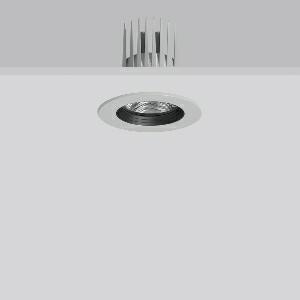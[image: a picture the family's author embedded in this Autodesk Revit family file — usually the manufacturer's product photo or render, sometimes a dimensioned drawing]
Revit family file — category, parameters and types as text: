
# Revit family: heledon_mini_e_901740_004_1_76_999f
name_source: partatom
category: Lighting Fixtures
units: mm (PartAtom-declared; Revit-internal decimal feet)

## family parameters
Cut with Voids When Loaded = No
Host = Face
Light Source = No
Part Type = Normal
Room Calculation Point = No
Round Connector Dimension = Use Diameter
Shared = No

## types (1)
- HELEDON mini E (1 x LED Modul 940, 2700 lm, 4000)
    Apparent Load = 20 VA
    Approval mark = CE
    CIE Flux Codes = 100 100 100 100 100
    Color Rendering = 92
    Color Temperature = 4000
    Default Elevation = 1800 mm
    Description = Series: HELEDON mini
Round recessed downlight. Housing: die-cast aluminium, powder-coated. Black plastic ring and recessed LED to prevent glare from the side. Optical assembly with reflector made of MIRO-Silver with 98% total light reflection for outstanding efficiency - can be changed without tools. Best colour rendering index Ra>90. Suitable for Recessed ceiling mounting. Installation without tools thanks to spring fastening system. Including separate LED converter with connecting cable 600 mm.High quality converter without flickering and stroboscopic effect. Through-wiring box (5 pole) available as accessory. The following accessories can be mounted without use of tools: interchangeable lenses, decorative glasses, honeycomb louvre, clear and frosted diffusers, white interchangeable plastic ring. 
Colour: silver
Diameter: 124 mm
Height: 3 mm
Cut-out diameter: 114 mm
Recess height: 170 mm
Luminaire: recess height: 120 mm
Lamp: LED
Socket: without socket
Colour temperature: 4000K
Colour rendering index (CRI): 92
System power: 20 W
Rated luminous flux: 2700 lm
Luminous efficiency: 135 lm/W
Control gear: Converter, dimmable, DALI
Protection class: II
Type of protection: IP 20
    Height = 0 mm  [stored 0 ft]
    Lamp = 1 x LED Modul 940
    Lamp Light Flux = 2700 lm
    Lamp count = 1
    Length = 124 mm  [stored 0.406824 ft]
    Lifetime = 50000 h
    Luminous efficacy = 135 lm/W
    Manufacturer = RZB
    ModVariant = No
    Model = 901740.004.1.76
    Mounting Place = Ceiling
    Mounting Type = Recessed
    Number of Poles = 1
    OnlyDefault = Yes
    Power Factor = 1
    Product Name = HELEDON mini E
    Product group = Recessed downlights
    ProductGroupID = 402
    Protection Class = Protection class II
    Protection Degree = IP 20
    RLX_Detail_Level = 1
    RLX_Emergency_Light_Flux = 0 lm
    RLX_Emergency_Type = 0
    RLX_Emergency_Type_DB = No
    RlxData = <blob elided: 129677 chars, md5=f038ff10>
    Socket = socket
    Standby Power = 0 W
    System Light Flux = 2700 lm
    System Power = 20 W
    Type Comments = Product without accessories
    Type Image = 901657.004.jpg
    URL = http://relux.com
    VarID = ---
    Voltage = 230 V
    Voltage Range = 220-240 V
    Weight = 0.00 kg
    Width = 0 mm  [stored 0 ft]

note: [stored X ft] marks values corroborated as IEEE doubles in the binary element streams (Revit-internal decimal feet)

## geometry (parser evidence)
native form markers: Blend x4, Sweep x10
no freeform markers — native parametric forms only
